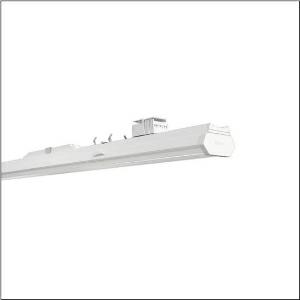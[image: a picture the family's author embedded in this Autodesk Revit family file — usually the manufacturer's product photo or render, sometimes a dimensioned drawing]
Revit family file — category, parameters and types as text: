
# Revit family: licross_11_protected_ho_51td1bdn4e5m
name_source: partatom
category: Lighting Fixtures
units: mm (PartAtom-declared; Revit-internal decimal feet)

## family parameters
Cut with Voids When Loaded = No
Host = Face
Light Source = No
Part Type = Normal
Room Calculation Point = No
Round Connector Dimension = Use Diameter
Shared = No

## types (1)
- --- (1 x LED, 14500 lm, 87.3 W, 4000K)
    Apparent Load = 87 VA
    CIE Flux Codes = 54 82 95 97 100
    Color Rendering = 80
    Color Temperature = 4000K
    Default Elevation = 1800 mm
    Description = Licross 11 Protected HO, luminaire insert, of sheet steel, galvanised, coil coated, white, length: 1.500mm, width: 90mm, height: 101mm, LED rated luminous flux: 14.500lm, light colour: 840, SDCM (Standard Deviation of Colour Matching)MacAdam ≤ 2 SDCM (initial), control gear: DALI 2, with plug, 5-pole, with phase selection, mains connection: 220..240V, AC, 50/60Hz, rated input power: 87W, internal wiring halogen-free, primary optical cover: cover, of PMMA, light emission: direct distribution, primary light characteristic: symmetric, protection rating (complete): IP54, insulation class (complete): insulation class I (protective earthing), certification: CE, ENEC, VDE, UKCA, protection symbol: D if used in an environment with non-conductive dust loads with corresponding accessories, impact resistance: IK06, permissible ambient temperature for indoor applications: -25..+30°C, corresponds to IFS (International Featured Standards) requirements for safety and quality in the food industry, reducing of maximum allowable ambient temperature of 5°C with ceiling mounting, LABS conformity tested according to VDMA 24364:2018-05, The light source and the operating device comply with the requirements of the Ecodesign Regulation (EU) 2019/2020 and are replaceable in accordance with this regulation, packaging unit: 1 piece
    Height = 92 mm
    Lamp = 1 x LED
    Lamp Light Flux = 14500 lm
    Lamp Power = 87.3 W
    Lamp count = 1
    Length = 1500 mm
    Luminous efficacy = 166 lm/W
    Manufacturer = Siteco
    ModVariant = No
    Model = 51TD1BDN4E5M
    Mounting Place = Ceiling
    Mounting Type = Pendant
    Number of Poles = 1
    OnlyDefault = Yes
    Power Factor = 1
    Product Name = Licross 11 Protected HO
    Product group = luminaire insert | ceiling pendant
    ProductGroupID = 901
    Protection Class = Protection class I
    Protection Degree = IP 54
    RLX_Detail_Level = 1
    RLX_Emergency_Light_Flux = 0 lm
    RLX_Emergency_Type = 0
    RLX_Emergency_Type_DB = No
    RlxData = <blob elided: 24637 chars, md5=eaa47a9c>
    Socket = socket
    Standby Power = 0 W
    System Light Flux = 14500 lm
    System Power = 87 W
    Type Comments = factory setting: luminous flux: 100 % | dim-lin: 254 | 589 mA
    Type Image = l_1256145.jpg
    URL = http://relux.com
    VarID = @adj_030417
    Voltage = 0 V
    Weight = 0.00 kg
    Width = 88 mm

## geometry (parser evidence)
native form markers: Blend x4, Sweep x11
no freeform markers — native parametric forms only
